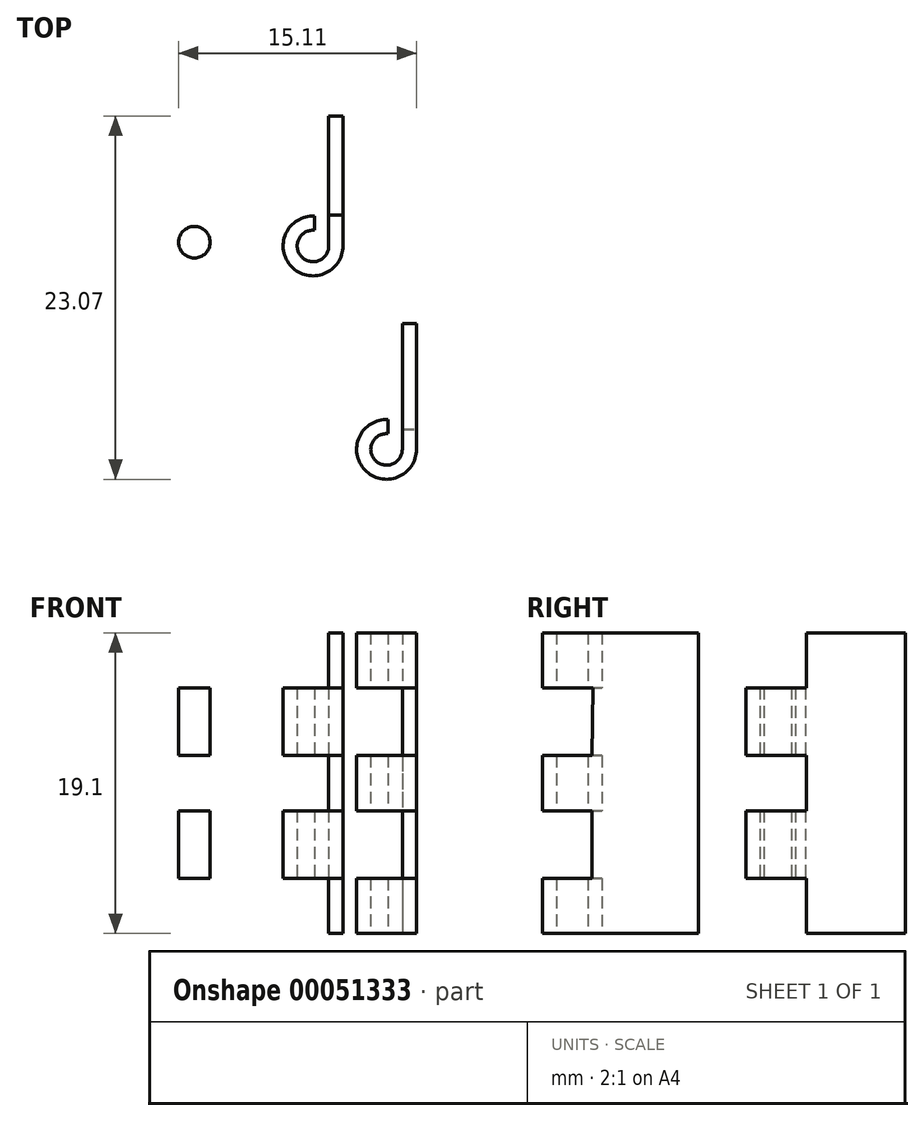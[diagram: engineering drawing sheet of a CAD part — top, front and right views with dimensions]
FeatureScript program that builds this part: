
annotation { "Feature Type Name" : "Feature", "Feature Type Description" : "" }
export const myFeature = defineFeature(function(context is Context, id is Id, definition is map)
    precondition{}
    {
        {
            var Q0;
            Q0=qCreatedBy(makeId("Top.planeOp"),FACE);
            var sketch = newSketch(context, id + "F0", { "sketchPlane" : qUnion([Q0])});
            skLineSegment(sketch, "E0", {"start": v(10.74, 8.67) * mm, "end": v(10.74, 0.67) * mm});
            skArc(sketch, "E1", {"start": v(10.74, 0.67) * mm, "mid": v(7.47, -0.65) * mm, "end": v(8.92, 2.56) * mm});
            skLineSegment(sketch, "E2", {"start": v(10.74, 8.67) * mm, "end": v(9.84, 8.67) * mm});
            skLineSegment(sketch, "E3", {"start": v(9.84, 8.67) * mm, "end": v(9.84, 0.67) * mm});
            skLineSegment(sketch, "E4", {"start": v(8.92, 2.56) * mm, "end": v(8.92, 1.66) * mm});
            skArc(sketch, "E5", {"start": v(9.84, 0.67) * mm, "mid": v(8.1, -0.01) * mm, "end": v(8.92, 1.66) * mm});
            skLineSegment(sketch, "E6", {"start": v(6.07, 21.84) * mm, "end": v(6.07, 13.59) * mm});
            skArc(sketch, "E7", {"start": v(6.07, 13.59) * mm, "mid": v(2.8, 12.28) * mm, "end": v(4.26, 15.49) * mm});
            skLineSegment(sketch, "E8", {"start": v(5.17, 21.84) * mm, "end": v(5.17, 13.59) * mm});
            skLineSegment(sketch, "E9", {"start": v(6.07, 21.84) * mm, "end": v(5.17, 21.84) * mm});
            skArc(sketch, "E10", {"start": v(5.17, 13.59) * mm, "mid": v(3.43, 12.91) * mm, "end": v(4.26, 14.59) * mm});
            skLineSegment(sketch, "E11", {"start": v(4.26, 15.49) * mm, "end": v(4.26, 14.59) * mm});
            skCircle(sketch, "E12", {"center": v(-3.37, 13.83) * mm, "radius": 1 * mm});
            skSolve(sketch);
        }
        {
            var Q0;
            Q0=makeQuery(id+"F0.imprint","IMPRINT",FACE,{"disambiguationData":[TD([[makeQuery(id+"F0.imprint","IMPRINT",EDGE,{"derivedFrom":sQuery(id+"F0.wireOp",EDGE,"E0")}),-1.0]])]});
            var Q1;
            Q1=makeQuery(id+"F0.imprint","IMPRINT",FACE,{"disambiguationData":[TD([[makeQuery(id+"F0.imprint","IMPRINT",EDGE,{"derivedFrom":sQuery(id+"F0.wireOp",EDGE,"E6")}),-1.0]])]});
            var Q2;
            Q2=makeQuery(id+"F0.imprint","IMPRINT",FACE,{"disambiguationData":[TD([[makeQuery(id+"F0.imprint","IMPRINT",EDGE,{"derivedFrom":sQuery(id+"F0.wireOp",EDGE,"E12")}),1.0]])]});
            extrude(context, id + "F1", {"entities" : qUnion([Q0, Q1, Q2]), "depth" : 19.1 * mm});
        }
        {
            var Q0;
            Q0=makeQuery(id+"F1.opExtrude","SWEPT_FACE",FACE,{"disambiguationData":[OSD([sQuery(id+"F0.wireOp",EDGE,"E0")])]});
            var sketch = newSketch(context, id + "F2", { "sketchPlane" : qUnion([Q0])});
            skPoint(sketch, "E13.end.orphan", {"position": v(1.97, 0) * mm});
            skLineSegment(sketch, "E14", {"start": v(1.97, 15.6) * mm, "end": v(-1.7, 15.6) * mm});
            skLineSegment(sketch, "E15", {"start": v(-1.7, 15.6) * mm, "end": v(-1.7, 11.3) * mm});
            skLineSegment(sketch, "E16", {"start": v(-1.7, 11.3) * mm, "end": v(1.93, 11.3) * mm});
            skLineSegment(sketch, "E17", {"start": v(1.93, 7.8) * mm, "end": v(-1.82, 7.8) * mm});
            skLineSegment(sketch, "E18", {"start": v(-1.82, 7.8) * mm, "end": v(-1.82, 3.5) * mm});
            skLineSegment(sketch, "E19", {"start": v(-1.82, 3.5) * mm, "end": v(1.93, 3.5) * mm});
            skLineSegment(sketch, "E20", {"start": v(1.97, 15.6) * mm, "end": v(1.93, 11.3) * mm});
            skLineSegment(sketch, "E21", {"start": v(1.93, 7.47) * mm, "end": v(1.93, 3.5) * mm});
            skLineSegment(sketch, "E22", {"start": v(1.96, 15.6) * mm, "end": v(1.94, 12.88) * mm, "construction": true});
            skPoint(sketch, "E23.end.orphan", {"position": v(1.97, 19.1) * mm});
            skPoint(sketch, "E24.orphan", {"position": v(1.97, 17.35) * mm});
            skLineSegment(sketch, "E25", {"start": v(1.93, 7.47) * mm, "end": v(1.93, 7.8) * mm});
            skSolve(sketch);
        }
        {
            var Q0;
            {var subQ0=sQuery(id+"F2.wireOp",EDGE,"E15");Q0=makeQuery(id+"F2.imprint","IMPRINT",FACE,{"disambiguationData":[TD([[makeQuery(id+"F2.imprint","IMPRINT",EDGE,{"derivedFrom":subQ0}),1.0]])]});}
            var Q1;
            {var subQ0=sQuery(id+"F2.wireOp",EDGE,"E20");Q1=makeQuery(id+"F2.imprint","IMPRINT",FACE,{"disambiguationData":[TD([[makeQuery(id+"F2.imprint","IMPRINT",EDGE,{"derivedFrom":subQ0}),-1.0]])]});}
            var Q2;
            {var subQ0=sQuery(id+"F2.wireOp",EDGE,"E18");Q2=makeQuery(id+"F2.imprint","IMPRINT",FACE,{"disambiguationData":[TD([[makeQuery(id+"F2.imprint","IMPRINT",EDGE,{"derivedFrom":subQ0}),1.0]])]});}
            var Q3;
            {var subQ0=sQuery(id+"F2.wireOp",EDGE,"E21");Q3=makeQuery(id+"F2.imprint","IMPRINT",FACE,{"disambiguationData":[TD([[makeQuery(id+"F2.imprint","IMPRINT",EDGE,{"derivedFrom":subQ0}),-1.0]])]});}
            extrude(context, id + "F3", {"entities" : qUnion([Q0, Q1, Q2, Q3]), "operationType" : NewBodyOperationType.REMOVE, "endBound" : BoundingType.THROUGH_ALL, "oppositeDirection" : true, "depth" : 25 * mm});
        }
        {
            var Q0;
            Q0=makeQuery(id+"F1.opExtrude","SWEPT_FACE",FACE,{"disambiguationData":[OSD([sQuery(id+"F0.wireOp",EDGE,"E6")])]});
            var sketch = newSketch(context, id + "F4", { "sketchPlane" : qUnion([Q0])});
            skLineSegment(sketch, "E26", {"start": v(15.54, 19.1) * mm, "end": v(15.54, 15.6) * mm});
            skLineSegment(sketch, "E27", {"start": v(15.54, 15.6) * mm, "end": v(10.9, 15.6) * mm});
            skLineSegment(sketch, "E28", {"start": v(10.9, 15.6) * mm, "end": v(10.9, 19.1) * mm});
            skLineSegment(sketch, "E29", {"start": v(10.9, 19.1) * mm, "end": v(15.54, 19.1) * mm});
            skLineSegment(sketch, "E30", {"start": v(15.39, 11.3) * mm, "end": v(11.96, 11.3) * mm});
            skLineSegment(sketch, "E31", {"start": v(11.96, 7.8) * mm, "end": v(15.39, 7.8) * mm});
            skLineSegment(sketch, "E32", {"start": v(15.39, 3.5) * mm, "end": v(11.1, 3.5) * mm});
            skLineSegment(sketch, "E33", {"start": v(11.1, 3.5) * mm, "end": v(11.1, 0) * mm});
            skLineSegment(sketch, "E34", {"start": v(11.1, 0) * mm, "end": v(15.39, 0) * mm});
            skLineSegment(sketch, "E35", {"start": v(11.96, 11.3) * mm, "end": v(10.82, 11.3) * mm});
            skLineSegment(sketch, "E36", {"start": v(10.82, 11.3) * mm, "end": v(10.82, 7.8) * mm});
            skLineSegment(sketch, "E37", {"start": v(10.82, 7.8) * mm, "end": v(11.96, 7.8) * mm});
            skLineSegment(sketch, "E38", {"start": v(15.54, 15.6) * mm, "end": v(15.54, 0) * mm});
            skLineSegment(sketch, "E39", {"start": v(15.54, 0) * mm, "end": v(15.39, 0) * mm});
            skLineSegment(sketch, "E40", {"start": v(15.39, 3.5) * mm, "end": v(15.54, 3.5) * mm});
            skLineSegment(sketch, "E41", {"start": v(15.39, 7.8) * mm, "end": v(15.54, 7.8) * mm});
            skLineSegment(sketch, "E42", {"start": v(15.39, 11.3) * mm, "end": v(15.54, 11.3) * mm});
            skSolve(sketch);
        }
        {
            var Q0;
            {var subQ0=sQuery(id+"F4.wireOp",EDGE,"E28");Q0=makeQuery(id+"F4.imprint","IMPRINT",FACE,{"disambiguationData":[TD([[makeQuery(id+"F4.imprint","IMPRINT",EDGE,{"derivedFrom":subQ0}),-1.0]])]});}
            var Q1;
            {var subQ0=sQuery(id+"F4.wireOp",EDGE,"E26");Q1=makeQuery(id+"F4.imprint","IMPRINT",FACE,{"disambiguationData":[TD([[makeQuery(id+"F4.imprint","IMPRINT",EDGE,{"derivedFrom":subQ0}),-1.0]])]});}
            var Q2;
            {var subQ0=sQuery(id+"F4.wireOp",EDGE,"E35");Q2=makeQuery(id+"F4.imprint","IMPRINT",FACE,{"disambiguationData":[TD([[makeQuery(id+"F4.imprint","IMPRINT",EDGE,{"derivedFrom":subQ0}),1.0]])]});}
            var Q3;
            {var subQ0=sQuery(id+"F4.wireOp",EDGE,"E41");Q3=makeQuery(id+"F4.imprint","IMPRINT",FACE,{"disambiguationData":[TD([[makeQuery(id+"F4.imprint","IMPRINT",EDGE,{"derivedFrom":subQ0}),1.0]])]});}
            var Q4;
            {var subQ0=sQuery(id+"F4.wireOp",EDGE,"E33");Q4=makeQuery(id+"F4.imprint","IMPRINT",FACE,{"disambiguationData":[TD([[makeQuery(id+"F4.imprint","IMPRINT",EDGE,{"derivedFrom":subQ0}),1.0]])]});}
            var Q5;
            {var subQ0=sQuery(id+"F4.wireOp",EDGE,"E39");Q5=makeQuery(id+"F4.imprint","IMPRINT",FACE,{"disambiguationData":[TD([[makeQuery(id+"F4.imprint","IMPRINT",EDGE,{"derivedFrom":subQ0}),-1.0]])]});}
            extrude(context, id + "F5", {"entities" : qUnion([Q0, Q1, Q2, Q3, Q4, Q5]), "operationType" : NewBodyOperationType.REMOVE, "endBound" : BoundingType.THROUGH_ALL, "oppositeDirection" : true, "depth" : 25 * mm});
        }
        {
            var Q0;
            Q0=makeQuery(id+"F3.boolean.opBoolean","COPY",FACE,{"disambiguationData":[TD([makeQuery(id+"F1.opExtrude","SWEPT_FACE",FACE,{"disambiguationData":[OSD([sQuery(id+"F0.wireOp",EDGE,"E1")])]})])],"derivedFrom":makeQuery(id+"F3.opExtrude","SWEPT_FACE",FACE,{"disambiguationData":[OSD([sQuery(id+"F2.wireOp",EDGE,"E20")])]})});
            var Q1;
            Q1=makeQuery(id+"F3.boolean.opBoolean","COPY",FACE,{"disambiguationData":[TD([makeQuery(id+"F1.opExtrude","SWEPT_FACE",FACE,{"disambiguationData":[OSD([sQuery(id+"F0.wireOp",EDGE,"E1")])]})])],"derivedFrom":makeQuery(id+"F3.opExtrude","SWEPT_FACE",FACE,{"disambiguationData":[OSD([sQuery(id+"F2.wireOp",EDGE,"E21"),sQuery(id+"F2.wireOp",EDGE,"E25")])]})});
            extrude(context, id + "F6", {"entities" : qUnion([Q0, Q1]), "operationType" : NewBodyOperationType.REMOVE, "endBound" : BoundingType.THROUGH_ALL, "oppositeDirection" : true, "depth" : 25 * mm});
        }
    });
